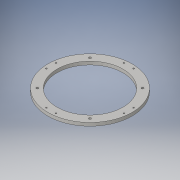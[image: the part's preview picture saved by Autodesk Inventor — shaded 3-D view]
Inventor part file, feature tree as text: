
AUTODESK INVENTOR PART (.ipt)
format: ipt  version: 2016 SP1 (Build 200210100, 210)  size: 126,976 bytes
history: native  units: in
note: dims shown in document units (in); Inventor stores cm internally (conversion verified against a paired STEP export)
features: sketch x3, hole x2, pattern_circular x2, extrude x1
ambient origin geometry x8: Origin, YZ Plane, XZ Plane, XY Plane, X Axis, Y Axis, Z Axis, Center Point
bodies: Solid1 (feature_tree)
feature tree (8):
  extrude  "Extrusion1"  Depth=10.2in
  hole  "Hole1"  [1 undecoded]
  pattern_circular  "Circular Pattern1"  Count=4 Angle=360.0deg
  hole  "Hole2"  [1 undecoded]
  pattern_circular  "Circular Pattern2"  Angle=45.0deg  [1 undecoded]
  sketch  "Sketch1"  dims[d0=13.0in d1=10.2in]
  sketch  "Sketch2"  dims[d2=0.5in d3=0.0in d6=6.0in]
  sketch  "Sketch3"  dims[d7=0.75in d8=0.211in d9=0.5in d10=0.507in d11=0.25in d12=0.5635in d13=0.679in d14=0.8108in d15=1.5748in d16=360.0deg d18=5.75in d19=45.0deg d20=0.332in d21=0.75in d22=0.635in d23=0.25in d24=0.5635in d25=1.0in d26=0.8108in d27=1.5748in d28=360.0deg]
note: 3 required parameter values undecoded (feature->parameter linkage not recoverable at this tier; creation-order binding heuristic only, values carry confidence <= 0.55)
